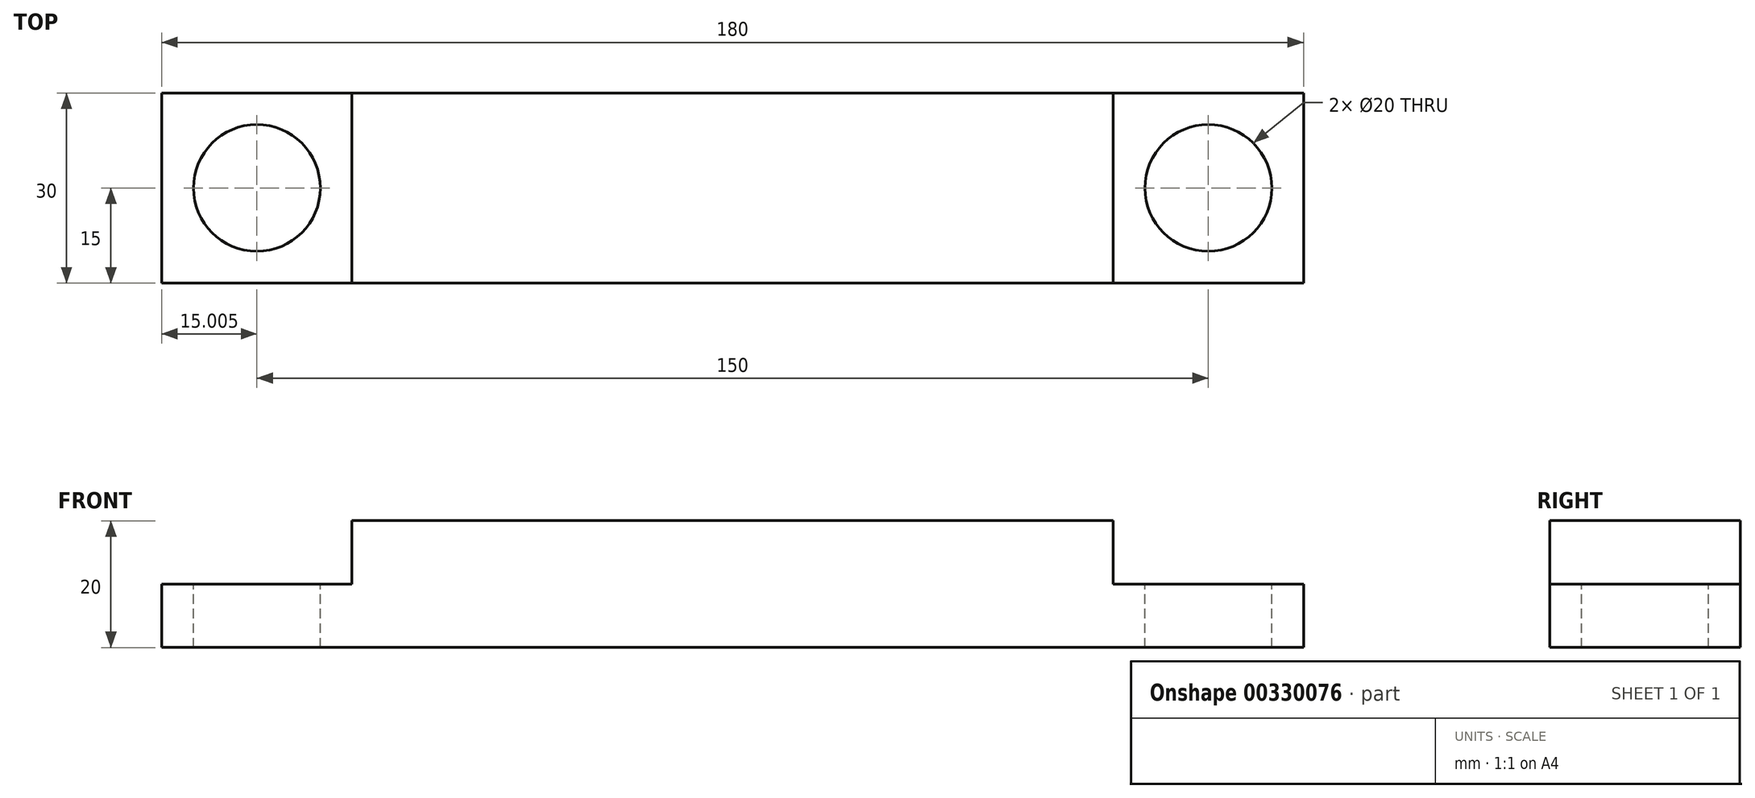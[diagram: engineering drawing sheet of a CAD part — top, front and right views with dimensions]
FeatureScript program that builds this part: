
annotation { "Feature Type Name" : "Feature", "Feature Type Description" : "" }
export const myFeature = defineFeature(function(context is Context, id is Id, definition is map)
    precondition{}
    {
        {
            var Q0;
            Q0=qCreatedBy(makeId("Front.planeOp"),FACE);
            var sketch = newSketch(context, id + "F0", { "sketchPlane" : qUnion([Q0])});
            skLineSegment(sketch, "E0", {"start": v(-91.38, 28.37) * mm, "end": v(88.62, 28.37) * mm});
            skLineSegment(sketch, "E1", {"start": v(88.62, 28.37) * mm, "end": v(88.62, 38.37) * mm});
            skLineSegment(sketch, "E2", {"start": v(58.62, 48.37) * mm, "end": v(-61.38, 48.37) * mm});
            skLineSegment(sketch, "E3", {"start": v(-91.38, 38.37) * mm, "end": v(-91.38, 28.37) * mm});
            skLineSegment(sketch, "E4", {"start": v(-91.38, 38.37) * mm, "end": v(-61.38, 38.37) * mm});
            skLineSegment(sketch, "E5", {"start": v(-61.38, 38.37) * mm, "end": v(-61.38, 48.37) * mm});
            skLineSegment(sketch, "E6", {"start": v(88.62, 38.37) * mm, "end": v(58.62, 38.37) * mm});
            skLineSegment(sketch, "E7", {"start": v(58.62, 38.37) * mm, "end": v(58.62, 48.37) * mm});
            skSolve(sketch);
        }
        {
            var Q0;
            Q0=qSketchRegion(id+"F0",true);
            extrude(context, id + "F1", {"entities" : qUnion([Q0]), "depth" : 30 * mm, "offsetDistance" : 25 * mm});
        }
        {
            var Q0;
            Q0=makeQuery(id+"F1.opExtrude","SWEPT_FACE",FACE,{"disambiguationData":[OSD([sQuery(id+"F0.wireOp",EDGE,"E6")])]});
            var sketch = newSketch(context, id + "F2", { "sketchPlane" : qUnion([Q0])});
            skLineSegment(sketch, "E8", {"start": v(88.62, -15) * mm, "end": v(83.62, -15) * mm});
            skLineSegment(sketch, "E9", {"start": v(73.62, 0) * mm, "end": v(73.62, -5) * mm});
            skCircle(sketch, "E10", {"center": v(73.62, -15) * mm, "radius": 10 * mm});
            skLineSegment(sketch, "E11.trimOffspring", {"start": v(73.62, -25) * mm, "end": v(73.62, -30) * mm});
            skLineSegment(sketch, "E12.trimOffspring", {"start": v(63.62, -15) * mm, "end": v(58.62, -15) * mm});
            skSolve(sketch);
        }
        {
            var Q0;
            Q0=makeQuery(id+"F1.opExtrude","SWEPT_FACE",FACE,{"disambiguationData":[OSD([sQuery(id+"F0.wireOp",EDGE,"E4")])]});
            var sketch = newSketch(context, id + "F3", { "sketchPlane" : qUnion([Q0])});
            skLineSegment(sketch, "E13", {"start": v(-61.38, -15) * mm, "end": v(-66.38, -15) * mm});
            skLineSegment(sketch, "E14", {"start": v(-76.38, 0) * mm, "end": v(-76.38, -5) * mm});
            skCircle(sketch, "E15", {"center": v(-76.38, -15) * mm, "radius": 10 * mm});
            skLineSegment(sketch, "E16.trimOffspring", {"start": v(-76.38, -25) * mm, "end": v(-76.38, -30) * mm});
            skLineSegment(sketch, "E17.trimOffspring", {"start": v(-86.38, -15) * mm, "end": v(-91.38, -15) * mm});
            skSolve(sketch);
        }
        {
            var Q0;
            {var subQ0=sQuery(id+"F3.wireOp",EDGE,"E15");var subQ1=makeQuery(id+"F3.imprint","INTERSECT",VERTEX,{"derivedFrom":[sQuery(id+"F3.wireOp",EDGE,"E13"),subQ0]});Q0=makeQuery(id+"F3.imprint","IMPRINT",FACE,{"disambiguationData":[TD([[makeQuery(id+"F3.imprint","IMPRINT",EDGE,{"disambiguationData":[TD([[subQ1,-1.0]])],"derivedFrom":subQ0}),1.0]])]});}
            extrude(context, id + "F4", {"entities" : qUnion([Q0]), "operationType" : NewBodyOperationType.REMOVE, "oppositeDirection" : true, "depth" : 25 * mm, "offsetDistance" : 25 * mm});
        }
        {
            var Q0;
            {var subQ0=sQuery(id+"F2.wireOp",EDGE,"E10");var subQ1=makeQuery(id+"F2.imprint","INTERSECT",VERTEX,{"derivedFrom":[sQuery(id+"F2.wireOp",EDGE,"E8"),subQ0]});Q0=makeQuery(id+"F2.imprint","IMPRINT",FACE,{"disambiguationData":[TD([[makeQuery(id+"F2.imprint","IMPRINT",EDGE,{"disambiguationData":[TD([[subQ1,-1.0]])],"derivedFrom":subQ0}),1.0]])]});}
            extrude(context, id + "F5", {"entities" : qUnion([Q0]), "operationType" : NewBodyOperationType.REMOVE, "oppositeDirection" : true, "depth" : 25 * mm, "offsetDistance" : 25 * mm});
        }
    });
